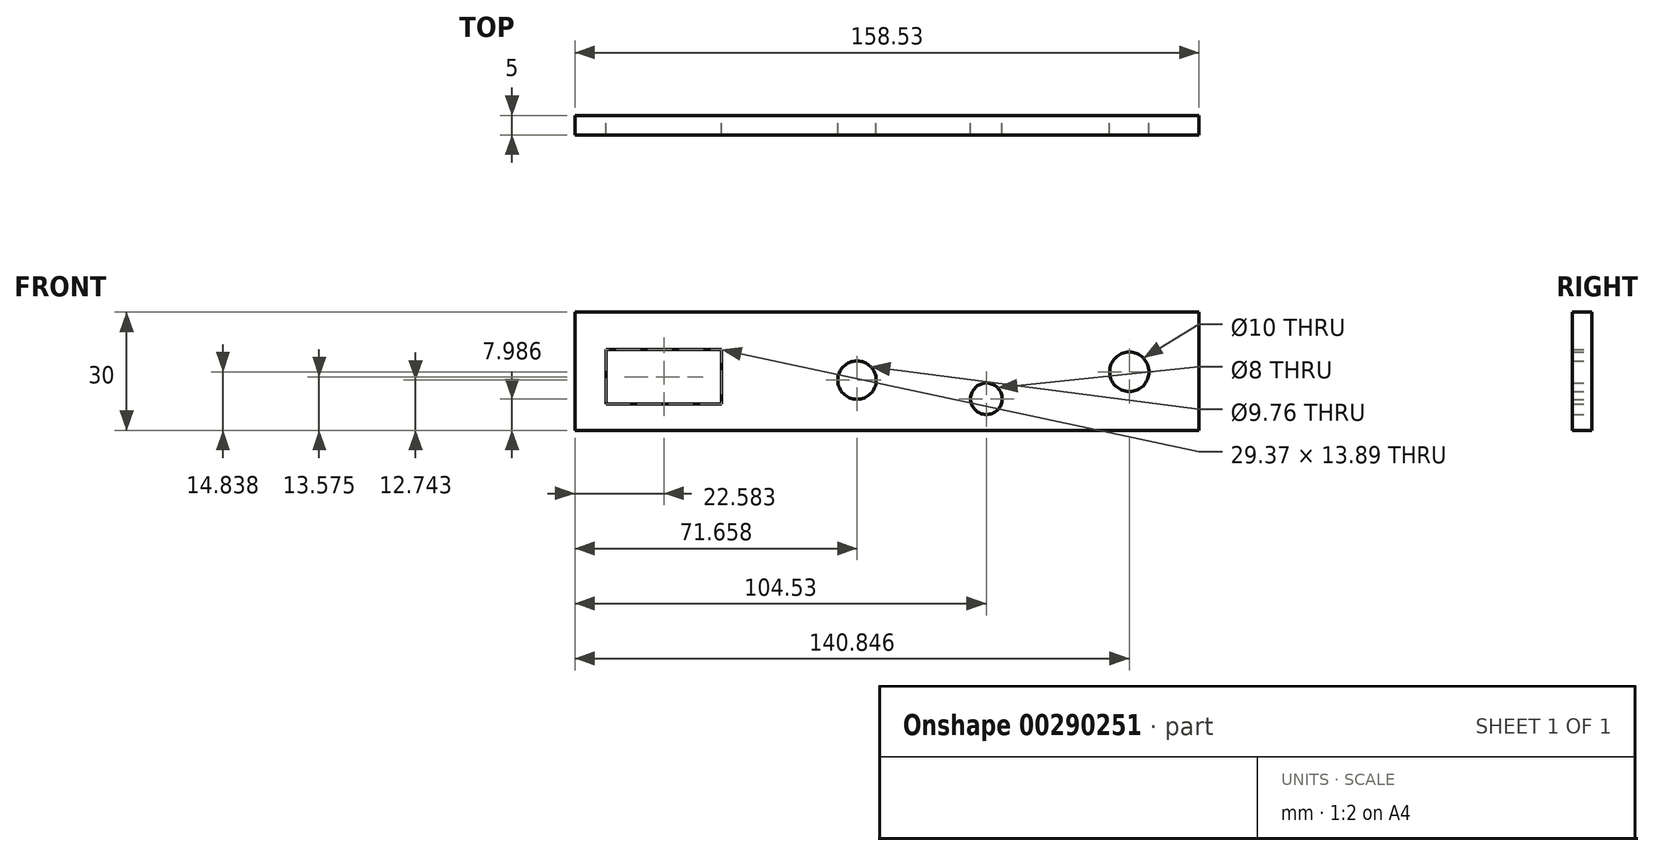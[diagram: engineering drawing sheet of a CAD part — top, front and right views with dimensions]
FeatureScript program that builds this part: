
annotation { "Feature Type Name" : "Feature", "Feature Type Description" : "" }
export const myFeature = defineFeature(function(context is Context, id is Id, definition is map)
    precondition{}
    {
        {
            var Q0;
            Q0=qCreatedBy(makeId("Front.planeOp"),FACE);
            var sketch = newSketch(context, id + "F0", { "sketchPlane" : qUnion([Q0])});
            skLineSegment(sketch, "E0", {"start": v(-104.53, 47.53) * mm, "end": v(-104.53, 17.53) * mm});
            skLineSegment(sketch, "E1", {"start": v(-104.53, 17.53) * mm, "end": v(54, 17.53) * mm});
            skLineSegment(sketch, "E2", {"start": v(54, 17.53) * mm, "end": v(54, 47.53) * mm});
            skLineSegment(sketch, "E3", {"start": v(54, 47.53) * mm, "end": v(-104.53, 47.53) * mm});
            skCircle(sketch, "E4", {"center": v(36.32, 32.37) * mm, "radius": 5 * mm});
            skCircle(sketch, "E5", {"center": v(0, 25.52) * mm, "radius": 4 * mm});
            skLineSegment(sketch, "E6.bottom", {"start": v(-67.26, 38.05) * mm, "end": v(-96.63, 38.05) * mm});
            skLineSegment(sketch, "E6.top", {"start": v(-67.26, 24.16) * mm, "end": v(-96.63, 24.16) * mm});
            skLineSegment(sketch, "E6.left", {"start": v(-67.26, 38.05) * mm, "end": v(-67.26, 24.16) * mm});
            skLineSegment(sketch, "E6.right", {"start": v(-96.63, 38.05) * mm, "end": v(-96.63, 24.16) * mm});
            skCircle(sketch, "E7", {"center": v(-32.87, 30.27) * mm, "radius": 4.88 * mm});
            skSolve(sketch);
        }
        {
            var Q0;
            Q0=makeQuery(id+"F0.imprint","IMPRINT",FACE,{"disambiguationData":[TD([[makeQuery(id+"F0.imprint","IMPRINT",EDGE,{"derivedFrom":sQuery(id+"F0.wireOp",EDGE,"E0")}),1.0]])]});
            extrude(context, id + "F1", {"entities" : qUnion([Q0]), "depth" : 5 * mm});
        }
    });
